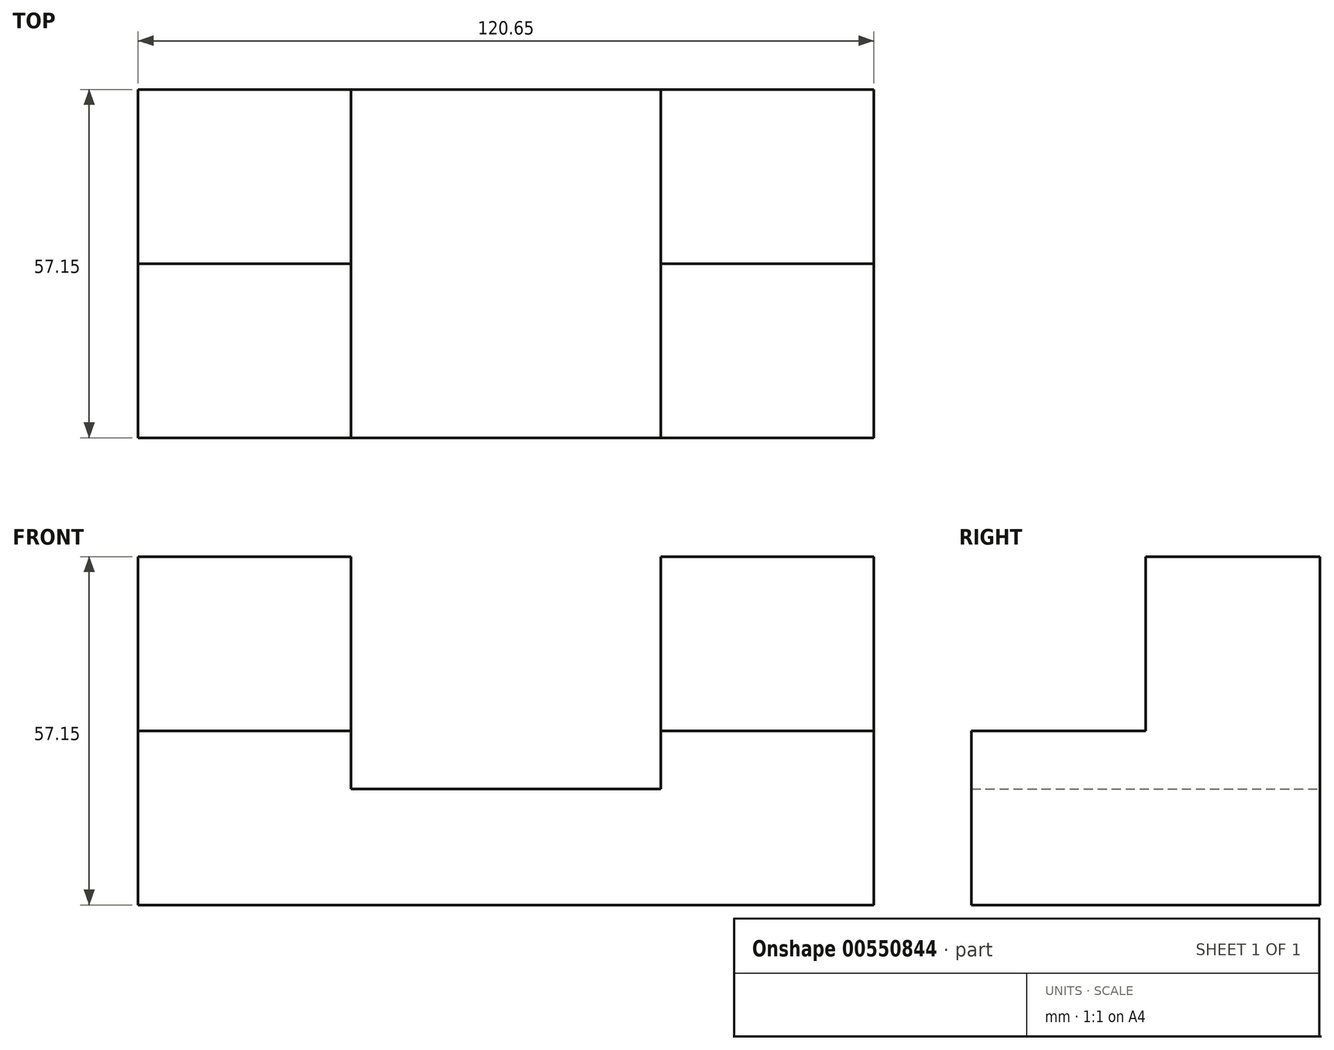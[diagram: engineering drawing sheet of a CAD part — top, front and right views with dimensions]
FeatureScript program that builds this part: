
annotation { "Feature Type Name" : "Feature", "Feature Type Description" : "" }
export const myFeature = defineFeature(function(context is Context, id is Id, definition is map)
    precondition{}
    {
        {
            var Q0;
            Q0=qCreatedBy(makeId("Front.planeOp"),FACE);
            var sketch = newSketch(context, id + "F0", { "sketchPlane" : qUnion([Q0])});
            skLineSegment(sketch, "E0", {"start": v(-60.12, -20.41) * mm, "end": v(60.53, -20.41) * mm});
            skLineSegment(sketch, "E1", {"start": v(-60.12, -20.41) * mm, "end": v(-60.12, 36.74) * mm});
            skLineSegment(sketch, "E2", {"start": v(60.53, -20.41) * mm, "end": v(60.53, 36.74) * mm});
            skLineSegment(sketch, "E3", {"start": v(-60.12, 36.74) * mm, "end": v(-25.2, 36.74) * mm});
            skLineSegment(sketch, "E4", {"start": v(60.53, 36.74) * mm, "end": v(25.6, 36.74) * mm});
            skLineSegment(sketch, "E5", {"start": v(-25.2, 36.74) * mm, "end": v(-25.2, -1.36) * mm});
            skLineSegment(sketch, "E6", {"start": v(25.6, 36.74) * mm, "end": v(25.6, -1.36) * mm});
            skLineSegment(sketch, "E7", {"start": v(-25.2, -1.36) * mm, "end": v(25.6, -1.36) * mm});
            skSolve(sketch);
        }
        {
            var Q0;
            Q0 = qSketchRegion(id + "F0", true);
            extrude(context, id + "F1", {"entities" : qUnion([Q0]), "depth" : 28.57 * mm, "offsetDistance" : 25.4 * mm});
        }
        {
            var Q0;
            Q0=makeQuery(id+"F1.opExtrude","CAP_FACE",FACE,{"disambiguationData":[OSD([sQuery(id+"F0.wireOp",EDGE,"E0"),sQuery(id+"F0.wireOp",EDGE,"E1"),sQuery(id+"F0.wireOp",EDGE,"E2"),sQuery(id+"F0.wireOp",EDGE,"E3"),sQuery(id+"F0.wireOp",EDGE,"E4"),sQuery(id+"F0.wireOp",EDGE,"E5"),sQuery(id+"F0.wireOp",EDGE,"E6"),sQuery(id+"F0.wireOp",EDGE,"E7")])],"isStart":false});
            var sketch = newSketch(context, id + "F2", { "sketchPlane" : qUnion([Q0])});
            skLineSegment(sketch, "E8", {"start": v(-60.12, -20.41) * mm, "end": v(-60.12, 8.16) * mm});
            skLineSegment(sketch, "E9", {"start": v(-60.12, 8.16) * mm, "end": v(-25.2, 8.16) * mm});
            skLineSegment(sketch, "E10", {"start": v(-25.2, 8.16) * mm, "end": v(-25.2, -1.36) * mm});
            skLineSegment(sketch, "E11", {"start": v(-25.2, -1.36) * mm, "end": v(25.6, -1.36) * mm});
            skLineSegment(sketch, "E12", {"start": v(25.6, -1.36) * mm, "end": v(25.6, 8.16) * mm});
            skLineSegment(sketch, "E13", {"start": v(25.6, 8.16) * mm, "end": v(60.53, 8.16) * mm});
            skLineSegment(sketch, "E14", {"start": v(60.53, 8.16) * mm, "end": v(60.53, -20.41) * mm});
            skLineSegment(sketch, "E15", {"start": v(60.53, -20.41) * mm, "end": v(-60.12, -20.41) * mm});
            skSolve(sketch);
        }
        {
            var Q0;
            Q0 = qSketchRegion(id + "F2", true);
            extrude(context, id + "F3", {"entities" : qUnion([Q0]), "operationType" : NewBodyOperationType.ADD, "depth" : 28.57 * mm, "offsetDistance" : 25.4 * mm});
        }
    });
